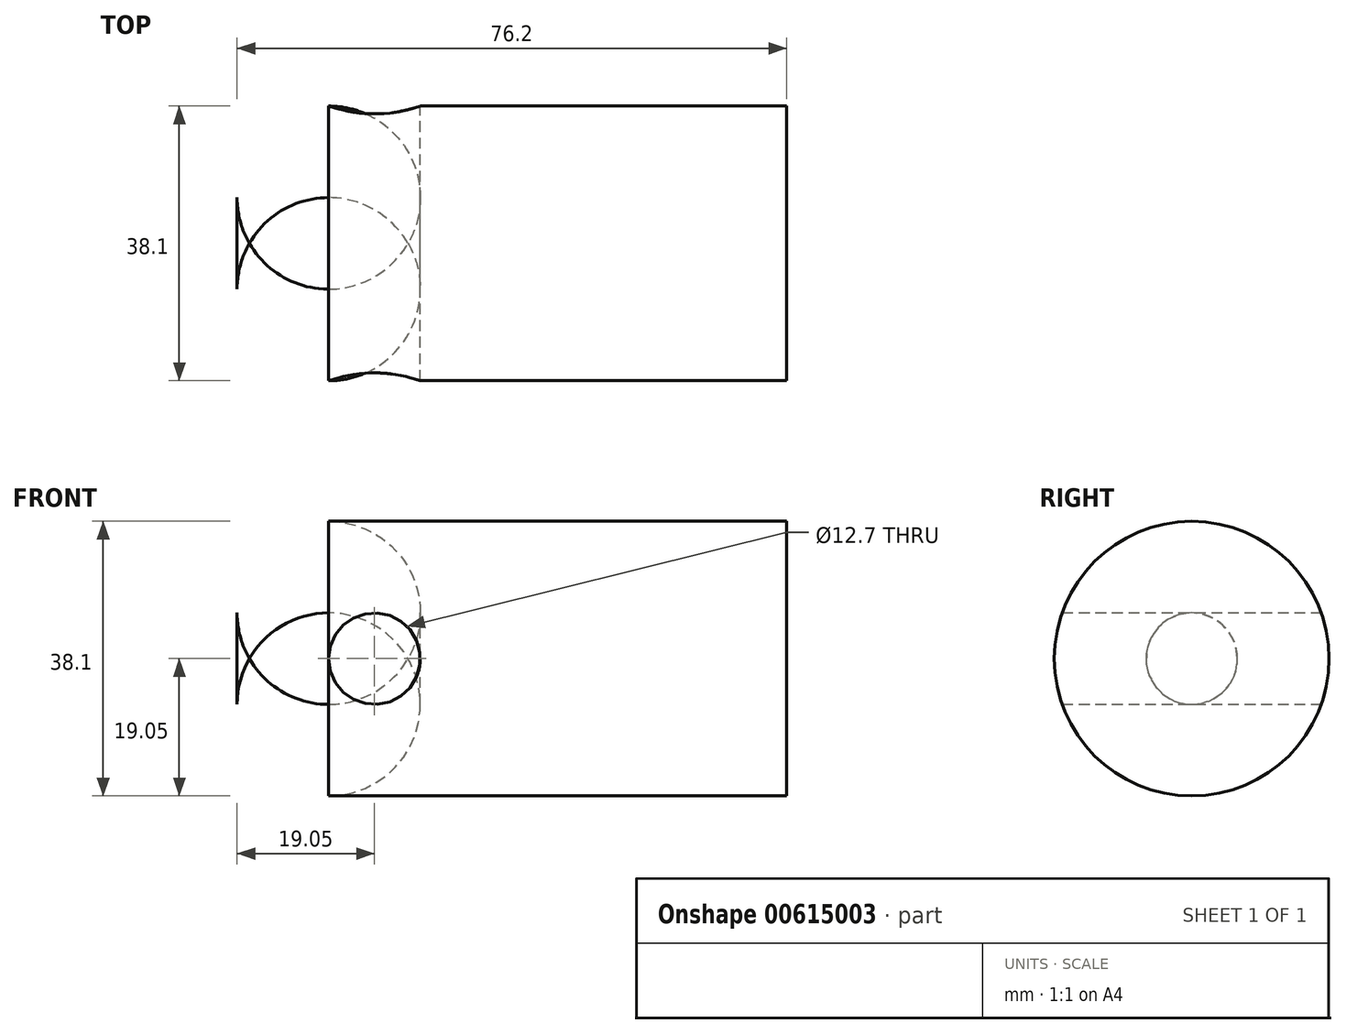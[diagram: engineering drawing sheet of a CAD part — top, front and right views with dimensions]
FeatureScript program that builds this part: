
annotation { "Feature Type Name" : "Feature", "Feature Type Description" : "" }
export const myFeature = defineFeature(function(context is Context, id is Id, definition is map)
    precondition{}
    {
        {
            var Q0;
            Q0=qCreatedBy(makeId("Right.planeOp"),FACE);
            var sketch = newSketch(context, id + "F0", { "sketchPlane" : qUnion([Q0])});
            skCircle(sketch, "E0", {"center": v(0, 0) * mm, "radius": 19.05 * mm});
            skSolve(sketch);
        }
        {
            var Q0;
            Q0=makeQuery(id+"F0.imprint","IMPRINT",FACE,{"disambiguationData":[TD([[makeQuery(id+"F0.imprint","IMPRINT",EDGE,{"derivedFrom":sQuery(id+"F0.wireOp",EDGE,"E0")}),1.0]])]});
            extrude(context, id + "F1", {"entities" : qUnion([Q0]), "endBound" : BoundingType.SYMMETRIC, "depth" : 50.8 * mm, "offsetDistance" : 25.4 * mm});
        }
        {
            var Q0;
            Q0=makeQuery(id+"F1.opExtrude","CAP_FACE",FACE,{"disambiguationData":[OSD([sQuery(id+"F0.wireOp",EDGE,"E0")])],"isStart":true});
            extrude(context, id + "F2", {"entities" : qUnion([Q0]), "operationType" : NewBodyOperationType.ADD, "depth" : 25.4 * mm, "offsetDistance" : 25.4 * mm});
        }
        {
            var Q0;
            Q0=qCreatedBy(makeId("Front.planeOp"),FACE);
            var sketch = newSketch(context, id + "F3", { "sketchPlane" : qUnion([Q0])});
            skCircle(sketch, "E1", {"center": v(-31.75, 0) * mm, "radius": 6.35 * mm});
            skSolve(sketch);
        }
        {
            var Q0;
            Q0=makeQuery(id+"F2.opExtrude","CAP_EDGE",EDGE,{"disambiguationData":[OSD([sQuery(id+"F0.wireOp",EDGE,"E0")])],"isStart":false});
            fillet(context, id + "F4", {"entities" : qUnion([Q0]), "radius" : 12.7 * mm, "tangentPropagation" : true, "allowEdgeOverflow" : false});
        }
        {
            var Q0;
            Q0 = qSketchRegion(id + "F3", true);
            extrude(context, id + "F5", {"entities" : qUnion([Q0]), "operationType" : NewBodyOperationType.REMOVE, "endBound" : BoundingType.SYMMETRIC, "depth" : 38.1 * mm, "offsetDistance" : 25.4 * mm});
        }
    });
